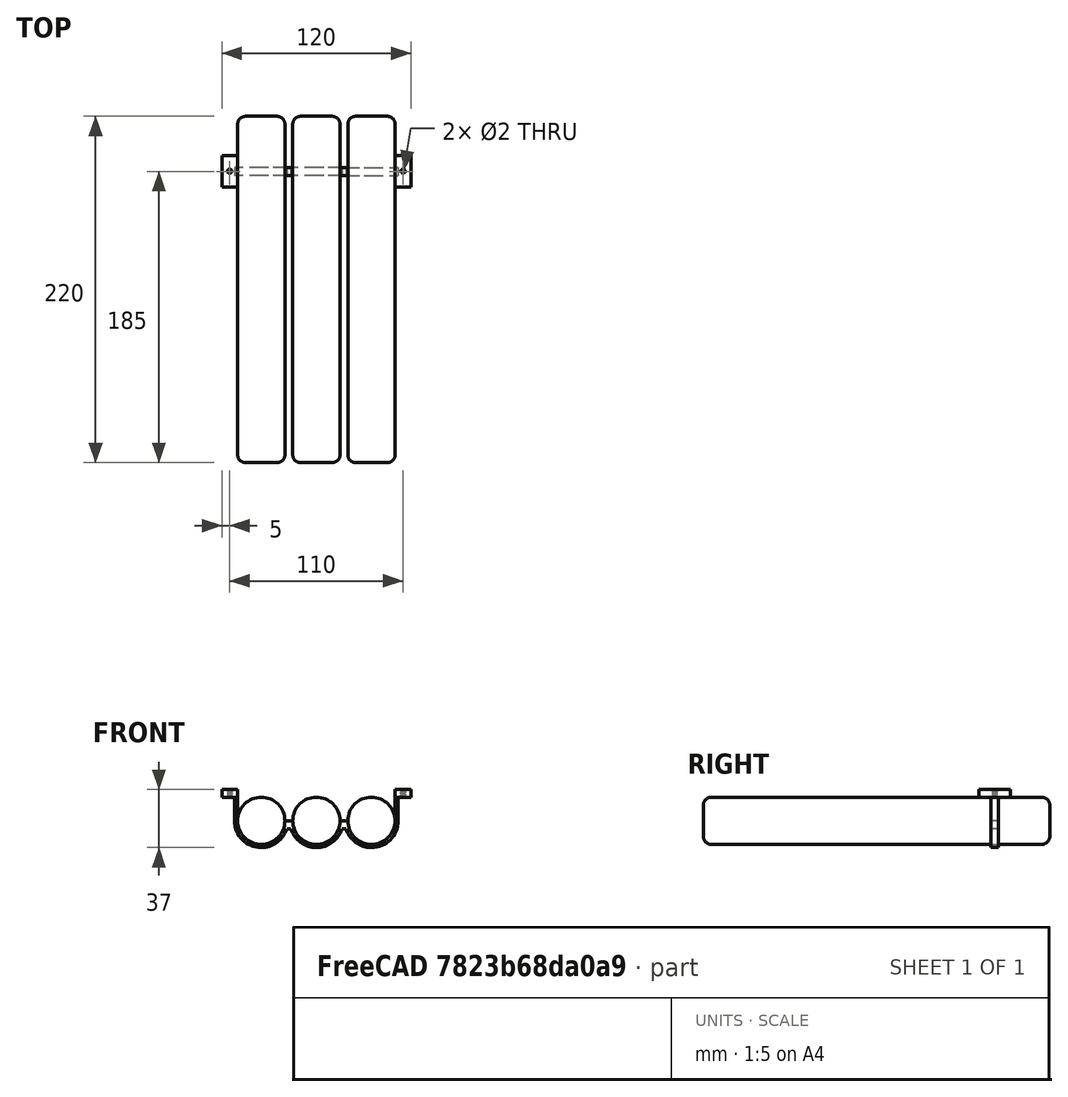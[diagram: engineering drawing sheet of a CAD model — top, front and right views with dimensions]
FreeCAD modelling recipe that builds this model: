
FCSTD DOCUMENT  (FreeCAD 0.21R33694 (Git))
Label: tanques-flotabilidad
License: Creative Commons Attribution-NonCommercial-ShareAlike 4.0
LicenseURL: https://creativecommons.org/licenses/by-nc-sa/4.0/
objects: TechDraw::DrawViewDimension×14, Part::Fuse×6, Part::Box×5, TechDraw::DrawViewPart×4, Part::Cylinder×3, Part::Fillet×3, Part::Mirroring×3, Part::Cut×3, TechDraw::DrawViewBalloon×3, Part::FeaturePython×2, Part::Feature×1, TechDraw::DrawSVGTemplate×1, TechDraw::DrawViewAnnotation×1, TechDraw::DrawPage×1
note: 47 computed .brp shape members not serialized (recipe doc carries the construction recipe); baked Part::Feature solids carry a one-line shape summary decoded from their .brp

FEATURE [Part::Box] Box026  label="flotadores"
  AttacherType = Attacher::AttachEngine3D
  Height = 5
  Length = 10
  Placement = pos=(-60,-85,0) rot=(0,0,1;0rad)
  Width = 20
FEATURE [Part::Box] Box027  label="Cube005"
  AttacherType = Attacher::AttachEngine3D
  Height = 20
  Length = 50
  Placement = pos=(-62,-97,-15) rot=(0,0,1;0rad)
  Width = 30
FEATURE [Part::Box] Box028  label="Cube006"
  AttacherType = Attacher::AttachEngine3D
  Height = 16
  Length = 2
  Placement = pos=(-52,-77.5,-15) rot=(0,0,1;0rad)
  Width = 5
FEATURE [Part::Box] Box030  label="Cube008"
  AttacherType = Attacher::AttachEngine3D
  Height = 20
  Length = 50
  Placement = pos=(-62,-97,-15) rot=(0,0,1;0rad)
  Width = 30
FEATURE [Part::Box] Box031  label="Cube009"
  AttacherType = Attacher::AttachEngine3D
  Height = 5
  Length = 5
  Placement = pos=(15,-77.5,-20) rot=(0,0,1;0rad)
  Width = 5
FEATURE [Part::Cylinder] Cylinder008  label="tanques"
  Angle = 360
  AttacherType = Attacher::AttachEngine3D
  FirstAngle = 0
  Height = 220
  Placement = pos=(-35,-110,-15) rot=(0.57735,-0.57735,-0.57735;4.18879rad)
  Radius = 15
  SecondAngle = 0
FEATURE [Part::Cylinder] Cylinder009  label="tanques001"
  Angle = 360
  AttacherType = Attacher::AttachEngine3D
  FirstAngle = 0
  Height = 220
  Placement = pos=(-35,-110,-15) rot=(0.57735,-0.57735,-0.57735;4.18879rad)
  Radius = 15
  SecondAngle = 0
FEATURE [Part::Cylinder] Cylinder010  label="tanques002"
  Angle = 360
  AttacherType = Attacher::AttachEngine3D
  FirstAngle = 0
  Height = 220
  Placement = pos=(-35,-110,-15) rot=(0.57735,-0.57735,-0.57735;4.18879rad)
  Radius = 15
  SecondAngle = 0
FEATURE [Part::Fillet] Fillet002  label="tanque"
  Base = -> Cylinder008
  Edges = 2 edges r=5: [Edge2,Edge3]
FEATURE [Part::Fillet] Fillet003  label="tanque001"
  Base = -> Cylinder009
  Edges = 2 edges r=5: [Edge2,Edge3]
  Placement = pos=(35,0,0) rot=(0,0,1;0rad)
FEATURE [Part::Fillet] Fillet004  label="tanque002"
  Base = -> Cylinder010
  Edges = 2 edges r=5: [Edge2,Edge3]
  Placement = pos=(70,0,0) rot=(0,0,1;0rad)
FEATURE [Part::Feature] Fusion001057  label="Rosca macho016"
  Placement = pos=(-55,-75,-5) rot=(0,0,1;0rad)
  shape: bbox 3.919 x 4.387 x 44 mm, 35 faces (baked)
FEATURE [Part::Mirroring] Part__Mirroring030  label="Cube009 (Mirror #13)"
  Base = (0,0,0)
  Normal = (1,0,0)
  Source = -> Box031
FEATURE [Part::Fuse] Fusion001059
  Base = -> Box031
  Refine = true
  Tool = -> Part__Mirroring030
FEATURE [Part::FeaturePython] Tube  # WARN: FeaturePython — macro-defined, semantics opaque (R4)
  AttacherType = Attacher::AttachEngine3D
  Height = 5
  InnerRadius = 15
  OuterRadius = 17
  Placement = pos=(-35,-77.5,-15) rot=(0.57735,-0.57735,-0.57735;4.18879rad)
FEATURE [Part::Cut] Cut039
  Base = -> Tube
  Refine = true
  Tool = -> Box027
FEATURE [Part::Fuse] Fusion001055
  Base = -> Cut039
  Refine = true
  Tool = -> Box028
FEATURE [Part::Fuse] Fusion001056  label="Flotador"
  Base = -> Box026
  Refine = true
  Tool = -> Fusion001055
FEATURE [Part::Cut] Cut042  label="flotadores001"
  Base = -> Fusion001056
  Refine = true
  Tool = -> Fusion001057
FEATURE [Part::Mirroring] Part__Mirroring028  label="flotadores001 (Mirror #11)"
  Base = (0,0,0)
  Normal = (1,0,0)
  Source = -> Cut042
FEATURE [Part::Fuse] Fusion001058
  Base = -> Cut042
  Refine = true
  Tool = -> Part__Mirroring028
FEATURE [Part::FeaturePython] Tube002  # WARN: FeaturePython — macro-defined, semantics opaque (R4)
  AttacherType = Attacher::AttachEngine3D
  Height = 5
  InnerRadius = 15
  OuterRadius = 17
  Placement = pos=(-35,-77.5,-15) rot=(0.57735,-0.57735,-0.57735;4.18879rad)
FEATURE [Part::Cut] Cut041
  Base = -> Tube002
  Placement = pos=(35,0,0) rot=(0,0,1;0rad)
  Refine = true
  Tool = -> Box030
FEATURE [Part::Fuse] Fusion001060
  Base = -> Cut041
  Refine = true
  Tool = -> Fusion001059
FEATURE [Part::Fuse] Fusion001061  label="sujecion-flotadores"
  Base = -> Fusion001058
  Refine = true
  Tool = -> Fusion001060
FEATURE [Part::Mirroring] Part__Mirroring031  label="sujecion-flotadores (Mirror #13)"
  Base = (0,0,0)
  Normal = (0,1,0)
  Source = -> Fusion001061
FEATURE [TechDraw::DrawSVGTemplate] Template
  Height = 297
  Orientation = 1
  Template = <path>
  Width = 420
FEATURE [TechDraw::DrawViewPart] View  label="Alzado"
  CoarseView = true
  Direction = (0,-1,0)
  Focus = 100
  HardHidden = false
  IsoCount = 0
  IsoHidden = false
  IsoVisible = false
  LockPosition = true
  Perspective = false
  Rotation = 0
  ScaleType = 0
  ScrubCount = 0
  SeamHidden = false
  SeamVisible = false
  SmoothHidden = false
  SmoothVisible = true
  Source = -> [Fusion001061]
  X = 110
  XDirection = (1,0,0)
  Y = 230
FEATURE [TechDraw::DrawViewPart] View001  label="Planta"
  CoarseView = true
  Direction = (0,0,1)
  Focus = 100
  HardHidden = false
  IsoCount = 0
  IsoHidden = false
  IsoVisible = false
  LockPosition = true
  Perspective = false
  Rotation = 0
  ScaleType = 0
  ScrubCount = 0
  SeamHidden = false
  SeamVisible = false
  SmoothHidden = false
  SmoothVisible = true
  Source = -> [Fusion001061]
  X = 110
  XDirection = (1,0,0)
  Y = 80
FEATURE [TechDraw::DrawViewPart] View002  label="Perfil"
  CoarseView = true
  Direction = (1,0,0)
  Focus = 100
  HardHidden = false
  IsoCount = 0
  IsoHidden = false
  IsoVisible = false
  LockPosition = true
  Perspective = false
  Rotation = 0
  ScaleType = 0
  ScrubCount = 0
  SeamHidden = false
  SeamVisible = false
  SmoothHidden = false
  SmoothVisible = true
  Source = -> [Fusion001061]
  X = 320
  XDirection = (0,1,0)
  Y = 230
FEATURE [TechDraw::DrawViewPart] View003  label="3DView"
  CoarseView = true
  Direction = (0.57735,-0.57735,0.57735)
  Focus = 100
  HardHidden = false
  IsoCount = 0
  IsoHidden = false
  IsoVisible = false
  LockPosition = true
  Perspective = false
  Rotation = 0
  ScaleType = 0
  ScrubCount = 0
  SeamHidden = false
  SeamVisible = false
  SmoothHidden = false
  SmoothVisible = true
  Source = -> [Fusion001061]
  X = 320
  XDirection = (0.707107,0.707107,0)
  Y = 130
FEATURE [TechDraw::DrawViewDimension] Dimension001
  AngleOverride = false
  Arbitrary = false
  ArbitraryTolerances = false
  EqualTolerance = true
  ExtensionAngle = 0
  FormatSpec = %.2w
  FormatSpecOverTolerance = %+.2w
  FormatSpecUnderTolerance = %+.2w
  Inverted = false
  LineAngle = 0
  LockPosition = false
  MeasureType = 1
  OverTolerance = 0
  References2D = -> [View]
  Rotation = 0
  ScaleType = 0
  TheoreticalExact = false
  Type = 1
  UnderTolerance = 0
  X = -18.2376
  Y = -16.7856
FEATURE [TechDraw::DrawViewDimension] Dimension003
  AngleOverride = false
  Arbitrary = false
  ArbitraryTolerances = false
  EqualTolerance = true
  ExtensionAngle = 0
  FormatSpec = %.2w
  FormatSpecOverTolerance = %+.2w
  FormatSpecUnderTolerance = %+.2w
  Inverted = false
  LineAngle = 0
  LockPosition = false
  MeasureType = 1
  OverTolerance = 0
  References2D = -> [View002]
  Rotation = 0
  ScaleType = 0
  TheoreticalExact = false
  Type = 1
  UnderTolerance = 0
  X = -0.678581
  Y = -33.2458
FEATURE [TechDraw::DrawViewDimension] Dimension004
  AngleOverride = false
  Arbitrary = false
  ArbitraryTolerances = false
  EqualTolerance = true
  ExtensionAngle = 0
  FormatSpec = %.2w
  FormatSpecOverTolerance = %+.2w
  FormatSpecUnderTolerance = %+.2w
  Inverted = false
  LineAngle = 0
  LockPosition = false
  MeasureType = 1
  OverTolerance = 0
  References2D = -> [View]
  Rotation = 0
  ScaleType = 0
  TheoreticalExact = false
  Type = 2
  UnderTolerance = 0
  X = -81.2594
  Y = 6.53298
FEATURE [TechDraw::DrawViewDimension] Dimension005
  AngleOverride = false
  Arbitrary = false
  ArbitraryTolerances = false
  EqualTolerance = true
  ExtensionAngle = 0
  FormatSpec = %.2w
  FormatSpecOverTolerance = %+.2w
  FormatSpecUnderTolerance = %+.2w
  Inverted = false
  LineAngle = 0
  LockPosition = false
  MeasureType = 1
  OverTolerance = 0
  References2D = -> [View002]
  Rotation = 0
  ScaleType = 0
  TheoreticalExact = false
  Type = 2
  UnderTolerance = 0
  X = -42.4558
  Y = 17.7624
FEATURE [TechDraw::DrawViewDimension] Dimension007
  AngleOverride = false
  Arbitrary = false
  ArbitraryTolerances = false
  EqualTolerance = true
  ExtensionAngle = 0
  FormatSpec = %.2w
  FormatSpecOverTolerance = %+.2w
  FormatSpecUnderTolerance = %+.2w
  Inverted = false
  LineAngle = 0
  LockPosition = false
  MeasureType = 1
  OverTolerance = 0
  References2D = -> [View]
  Rotation = 0
  ScaleType = 0
  TheoreticalExact = false
  Type = 1
  UnderTolerance = 0
  X = -46.8719
  Y = 12.4911
FEATURE [TechDraw::DrawViewDimension] Dimension008
  AngleOverride = false
  Arbitrary = false
  ArbitraryTolerances = false
  EqualTolerance = true
  ExtensionAngle = 0
  FormatSpec = %.2w
  FormatSpecOverTolerance = %+.2w
  FormatSpecUnderTolerance = %+.2w
  Inverted = false
  LineAngle = 0
  LockPosition = false
  MeasureType = 1
  OverTolerance = 0
  References2D = -> [View001]
  Rotation = 0
  ScaleType = 0
  TheoreticalExact = false
  Type = 1
  UnderTolerance = 0
  X = -56.0769
  Y = 26.141
FEATURE [TechDraw::DrawViewDimension] Dimension009
  AngleOverride = false
  Arbitrary = false
  ArbitraryTolerances = false
  EqualTolerance = true
  ExtensionAngle = 0
  FormatSpec = %.2w
  FormatSpecOverTolerance = %+.2w
  FormatSpecUnderTolerance = %+.2w
  Inverted = false
  LineAngle = 0
  LockPosition = false
  MeasureType = 1
  OverTolerance = 0
  References2D = -> [View001]
  Rotation = 0
  ScaleType = 0
  TheoreticalExact = false
  Type = 2
  UnderTolerance = 0
  X = 67.8974
  Y = 2.14102
FEATURE [TechDraw::DrawViewDimension] Dimension
  AngleOverride = false
  Arbitrary = false
  ArbitraryTolerances = false
  EqualTolerance = true
  ExtensionAngle = 0
  FormatSpec = %.2w
  FormatSpecOverTolerance = %+.2w
  FormatSpecUnderTolerance = %+.2w
  Inverted = false
  LineAngle = 0
  LockPosition = false
  MeasureType = 1
  OverTolerance = 0
  References2D = -> [View]
  Rotation = 0
  ScaleType = 0
  TheoreticalExact = false
  Type = 1
  UnderTolerance = 0
  X = -17.141
  Y = 9.61539
FEATURE [TechDraw::DrawViewDimension] Dimension010
  AngleOverride = false
  Arbitrary = false
  ArbitraryTolerances = false
  EqualTolerance = true
  ExtensionAngle = 0
  FormatSpec = %.2w
  FormatSpecOverTolerance = %+.2w
  FormatSpecUnderTolerance = %+.2w
  Inverted = false
  LineAngle = 0
  LockPosition = false
  MeasureType = 1
  OverTolerance = 0
  References2D = -> [View]
  Rotation = 0
  ScaleType = 0
  TheoreticalExact = false
  Type = 2
  UnderTolerance = 0
  X = 27.6975
  Y = -1.04706
FEATURE [TechDraw::DrawViewDimension] Dimension011
  AngleOverride = false
  Arbitrary = false
  ArbitraryTolerances = false
  EqualTolerance = true
  ExtensionAngle = 0
  FormatSpec = %.2w
  FormatSpecOverTolerance = %+.2w
  FormatSpecUnderTolerance = %+.2w
  Inverted = false
  LineAngle = 0
  LockPosition = false
  MeasureType = 1
  OverTolerance = 0
  References2D = -> [View002]
  Rotation = 0
  ScaleType = 0
  TheoreticalExact = false
  Type = 1
  UnderTolerance = 0
  X = -5.76779
  Y = 29.3812
FEATURE [TechDraw::DrawViewDimension] Dimension012
  AngleOverride = false
  Arbitrary = false
  ArbitraryTolerances = false
  EqualTolerance = true
  ExtensionAngle = 0
  FormatSpec = %.2w
  FormatSpecOverTolerance = %+.2w
  FormatSpecUnderTolerance = %+.2w
  Inverted = false
  LineAngle = 0
  LockPosition = false
  MeasureType = 1
  OverTolerance = 0
  References2D = -> [View001]
  Rotation = 0
  ScaleType = 0
  TheoreticalExact = false
  Type = 1
  UnderTolerance = 0
  X = -32.7858
  Y = 48.7119
FEATURE [TechDraw::DrawViewDimension] Dimension013
  AngleOverride = false
  Arbitrary = false
  ArbitraryTolerances = false
  EqualTolerance = true
  ExtensionAngle = 0
  FormatSpec = %.2w
  FormatSpecOverTolerance = %+.2w
  FormatSpecUnderTolerance = %+.2w
  Inverted = false
  LineAngle = 0
  LockPosition = false
  MeasureType = 1
  OverTolerance = 0
  References2D = -> [View001]
  Rotation = 0
  ScaleType = 0
  TheoreticalExact = false
  Type = 1
  UnderTolerance = 0
  X = -0.170321
  Y = 48.5416
FEATURE [TechDraw::DrawViewDimension] Dimension014
  AngleOverride = false
  Arbitrary = false
  ArbitraryTolerances = false
  EqualTolerance = true
  ExtensionAngle = 0
  FormatSpec = %.2w
  FormatSpecOverTolerance = %+.2w
  FormatSpecUnderTolerance = %+.2w
  Inverted = false
  LineAngle = 0
  LockPosition = false
  MeasureType = 1
  OverTolerance = 0
  References2D = -> [View001]
  Rotation = 0
  ScaleType = 0
  TheoreticalExact = false
  Type = 1
  UnderTolerance = 0
  X = 32.9561
  Y = 48.8822
FEATURE [TechDraw::DrawViewDimension] Dimension015
  AngleOverride = false
  Arbitrary = false
  ArbitraryTolerances = false
  EqualTolerance = true
  ExtensionAngle = 0
  FormatSpec = %.2w
  FormatSpecOverTolerance = %+.2w
  FormatSpecUnderTolerance = %+.2w
  Inverted = false
  LineAngle = 0
  LockPosition = false
  MeasureType = 1
  OverTolerance = 0
  References2D = -> [View001]
  Rotation = 0
  ScaleType = 0
  TheoreticalExact = false
  Type = 1
  UnderTolerance = 0
  X = -1.06451
  Y = -24.7983
FEATURE [TechDraw::DrawViewBalloon] Balloon
  BubbleShape = 0
  EndType = 0
  EndTypeScale = 1
  KinkLength = 5
  LockPosition = false
  OriginX = -21.8546
  OriginY = 9.71666
  Rotation = 0
  ScaleType = 0
  ShapeScale = 1
  SourceView = -> View003
  Text = 1
  TextWrapLen = -1
  X = -1.85463
  Y = 29.7167
FEATURE [TechDraw::DrawViewBalloon] Balloon001
  BubbleShape = 0
  EndType = 0
  EndTypeScale = 1
  KinkLength = 5
  LockPosition = false
  OriginX = 2.60604
  OriginY = -9.07914
  Rotation = 0
  ScaleType = 0
  ShapeScale = 1
  SourceView = -> View003
  Text = 2
  TextWrapLen = -1
  X = 21.3821
  Y = 17.4486
FEATURE [TechDraw::DrawViewBalloon] Balloon002
  BubbleShape = 0
  EndType = 0
  EndTypeScale = 1
  KinkLength = 5
  LockPosition = false
  OriginX = 23.8123
  OriginY = -20.3591
  Rotation = 0
  ScaleType = 0
  ShapeScale = 1
  SourceView = -> View003
  Text = 3
  TextWrapLen = -1
  X = 45.4442
  Y = 5.76069
FEATURE [TechDraw::DrawViewAnnotation] Annotation
  Font = osifont
  LineSpace = 100
  LockPosition = false
  MaxWidth = -1
  Rotation = 0
  ScaleType = 0
  Text = 1: Tanque de flotación izquierdo | 2: Tanque de flotación central | 3: Tanque de flotación derecho
  TextSize = 5
  TextStyle = 0
  X = 218.568
  Y = 151.764
FEATURE [TechDraw::DrawPage] Page  label="Planos-floating-tank"
  KeepUpdated = true
  NextBalloonIndex = 4
  ProjectionType = 0
  Template = -> Template
  Views = -> [View,View001,View002,View003,Dimension001,Dimension003,Dimension004,Dimension005,Dimension007,Dimension008,Dimension009,Dimension,Dimension010,Dimension011,Dimension012,Dimension013,Dimension014,Dimension015,Balloon,Balloon001,Balloon002,Annotation]
note: 1 file-system path scrubbed to <path> (originals preserved in the JSON sidecar)
